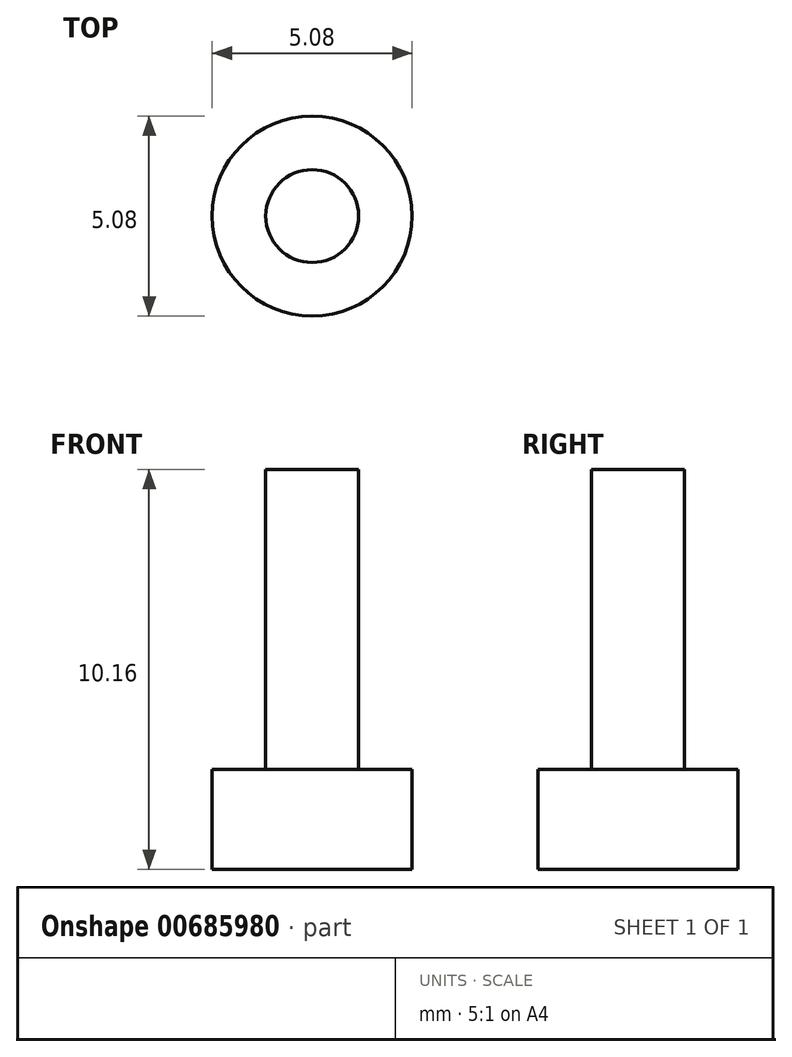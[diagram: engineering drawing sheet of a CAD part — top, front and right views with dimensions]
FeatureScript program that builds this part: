
annotation { "Feature Type Name" : "Feature", "Feature Type Description" : "" }
export const myFeature = defineFeature(function(context is Context, id is Id, definition is map)
    precondition{}
    {
        {
            var Q0;
            Q0=qCreatedBy(makeId("Top.planeOp"),FACE);
            var sketch = newSketch(context, id + "F0", { "sketchPlane" : qUnion([Q0])});
            skCircle(sketch, "E0", {"center": v(0, 0) * mm, "radius": 2.54 * mm});
            skSolve(sketch);
        }
        {
            var Q0;
            Q0=makeQuery(id+"F0.imprint","IMPRINT",FACE,{"disambiguationData":[TD([[makeQuery(id+"F0.imprint","IMPRINT",EDGE,{"derivedFrom":sQuery(id+"F0.wireOp",EDGE,"E0")}),1.0]])]});
            var Q1;
            Q1=sQuery(id+"F0.wireOp",EDGE,"E0");
            extrude(context, id + "F1", {"entities" : qUnion([Q0]), "surfaceEntities" : qUnion([Q1]), "depth" : 2.54 * mm, "offsetDistance" : 25.4 * mm});
        }
        {
            var Q0;
            Q0=makeQuery(id+"F1.opExtrude","CAP_FACE",FACE,{"disambiguationData":[OSD([sQuery(id+"F0.wireOp",EDGE,"E0")])],"isStart":false});
            var sketch = newSketch(context, id + "F2", { "sketchPlane" : qUnion([Q0])});
            skCircle(sketch, "E1", {"center": v(0, 0) * mm, "radius": 1.18 * mm});
            skSolve(sketch);
        }
        {
            var Q0;
            Q0=makeQuery(id+"F2.imprint","IMPRINT",FACE,{"disambiguationData":[TD([[makeQuery(id+"F2.imprint","IMPRINT",EDGE,{"derivedFrom":sQuery(id+"F2.wireOp",EDGE,"E1")}),1.0]])]});
            var Q1;
            Q1=sQuery(id+"F2.wireOp",EDGE,"E1");
            extrude(context, id + "F3", {"entities" : qUnion([Q0]), "operationType" : NewBodyOperationType.ADD, "surfaceEntities" : qUnion([Q1]), "depth" : 7.62 * mm, "offsetDistance" : 25.4 * mm});
        }
    });
